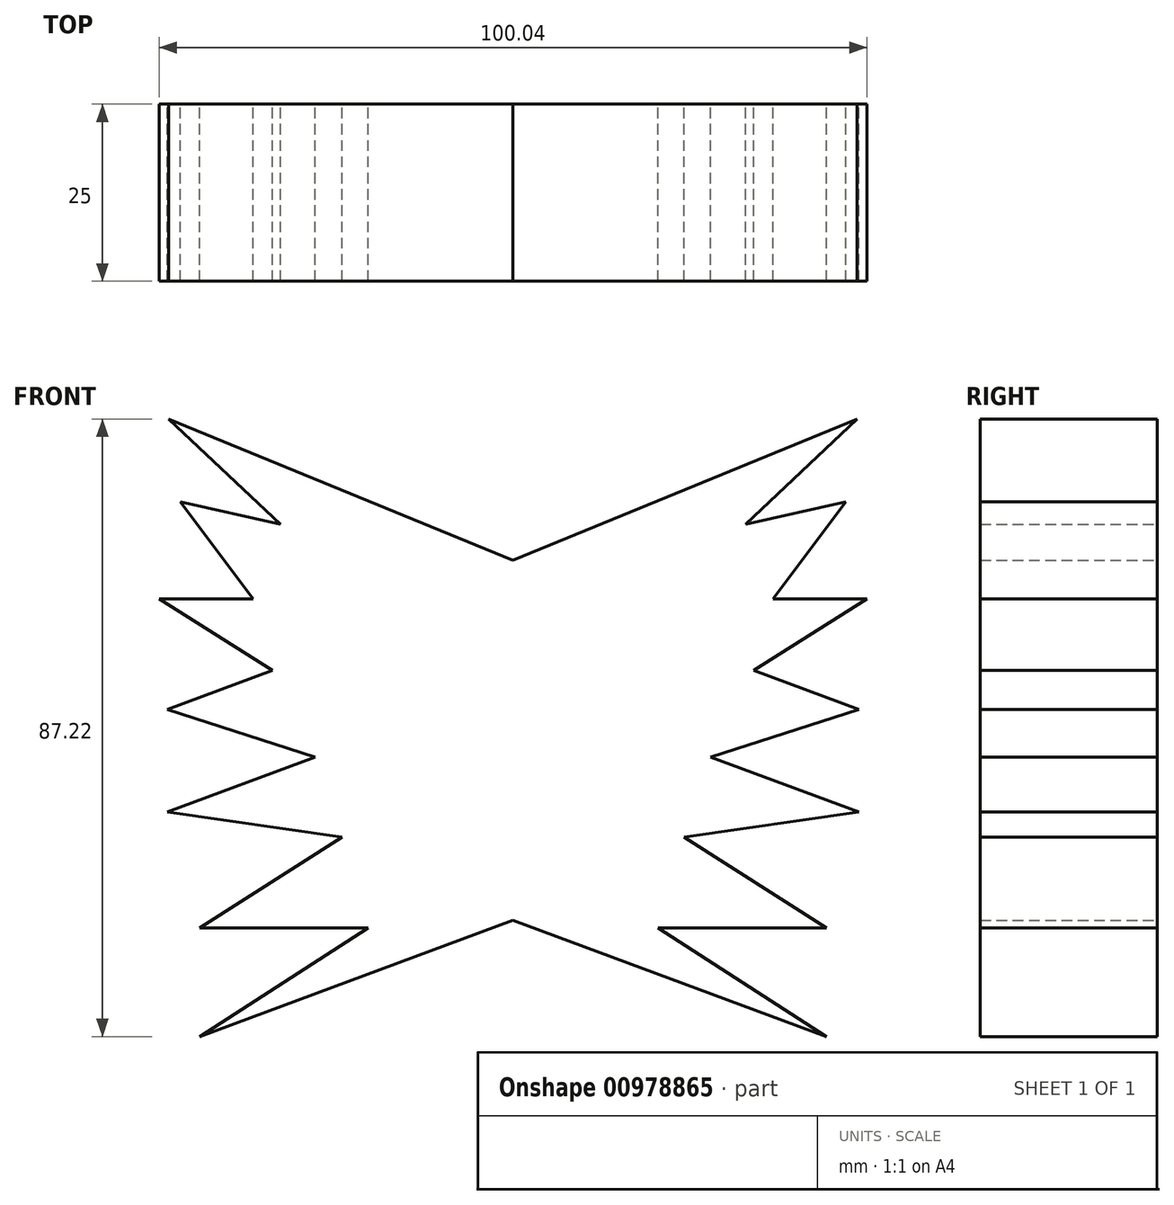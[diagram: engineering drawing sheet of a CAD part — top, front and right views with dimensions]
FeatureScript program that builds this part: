
annotation { "Feature Type Name" : "Feature", "Feature Type Description" : "" }
export const myFeature = defineFeature(function(context is Context, id is Id, definition is map)
    precondition{}
    {
        {
            var Q0;
            Q0=qCreatedBy(makeId("Front.planeOp"),FACE);
            var sketch = newSketch(context, id + "F0", { "sketchPlane" : qUnion([Q0])});
            skLineSegment(sketch, "E0", {"start": v(0, 35.6) * mm, "end": v(-48.65, 55.51) * mm});
            skLineSegment(sketch, "E1", {"start": v(-48.65, 55.51) * mm, "end": v(-32.85, 40.63) * mm});
            skLineSegment(sketch, "E2", {"start": v(-32.85, 40.63) * mm, "end": v(-47.04, 43.84) * mm});
            skLineSegment(sketch, "E3", {"start": v(-47.04, 43.84) * mm, "end": v(-36.74, 30.1) * mm});
            skLineSegment(sketch, "E4", {"start": v(-36.74, 30.1) * mm, "end": v(-50.02, 30.1) * mm});
            skLineSegment(sketch, "E5", {"start": v(-50.02, 30.1) * mm, "end": v(-34, 20.03) * mm});
            skLineSegment(sketch, "E6", {"start": v(-34, 20.03) * mm, "end": v(-48.88, 14.52) * mm});
            skLineSegment(sketch, "E7", {"start": v(-48.88, 14.52) * mm, "end": v(-27.94, 7.75) * mm});
            skLineSegment(sketch, "E8", {"start": v(-27.94, 7.75) * mm, "end": v(-48.88, 0) * mm});
            skLineSegment(sketch, "E9", {"start": v(-48.88, 0) * mm, "end": v(-24.15, -3.55) * mm});
            skLineSegment(sketch, "E10", {"start": v(-24.15, -3.55) * mm, "end": v(-44.3, -16.37) * mm});
            skLineSegment(sketch, "E11", {"start": v(-44.3, -16.37) * mm, "end": v(-20.49, -16.37) * mm});
            skLineSegment(sketch, "E12", {"start": v(-20.49, -16.37) * mm, "end": v(-44.3, -31.7) * mm});
            skLineSegment(sketch, "E13", {"start": v(-44.3, -31.7) * mm, "end": v(0, -15.31) * mm});
            skLineSegment(sketch, "E14", {"start": v(0, 60.32) * mm, "end": v(0, -32.62) * mm});
            skLineSegment(sketch, "E15.MirrorCS", {"start": v(0, 35.6) * mm, "end": v(48.65, 55.51) * mm});
            skLineSegment(sketch, "E16.MirrorCS", {"start": v(48.65, 55.51) * mm, "end": v(32.85, 40.63) * mm});
            skLineSegment(sketch, "E17.MirrorCS", {"start": v(32.85, 40.63) * mm, "end": v(47.04, 43.84) * mm});
            skLineSegment(sketch, "E18.MirrorCS", {"start": v(47.04, 43.84) * mm, "end": v(36.74, 30.1) * mm});
            skLineSegment(sketch, "E19.MirrorCS", {"start": v(36.74, 30.1) * mm, "end": v(50.02, 30.1) * mm});
            skLineSegment(sketch, "E20.MirrorCS", {"start": v(50.02, 30.1) * mm, "end": v(34, 20.03) * mm});
            skLineSegment(sketch, "E21.MirrorCS", {"start": v(34, 20.03) * mm, "end": v(48.88, 14.52) * mm});
            skLineSegment(sketch, "E22.MirrorCS", {"start": v(48.88, 14.52) * mm, "end": v(27.94, 7.75) * mm});
            skLineSegment(sketch, "E23.MirrorCS", {"start": v(27.94, 7.75) * mm, "end": v(48.88, 0) * mm});
            skLineSegment(sketch, "E24.MirrorCS", {"start": v(48.88, 0) * mm, "end": v(24.15, -3.55) * mm});
            skLineSegment(sketch, "E25.MirrorCS", {"start": v(24.15, -3.55) * mm, "end": v(44.3, -16.37) * mm});
            skLineSegment(sketch, "E26.MirrorCS", {"start": v(44.3, -16.37) * mm, "end": v(20.49, -16.37) * mm});
            skLineSegment(sketch, "E27.MirrorCS", {"start": v(20.49, -16.37) * mm, "end": v(44.3, -31.7) * mm});
            skLineSegment(sketch, "E28.MirrorCS", {"start": v(44.3, -31.7) * mm, "end": v(0, -15.31) * mm});
            skSolve(sketch);
        }
        {
            var Q0;
            {var subQ0=sQuery(id+"F0.wireOp",EDGE,"E15.MirrorCS");Q0=makeQuery(id+"F0.imprint","IMPRINT",FACE,{"disambiguationData":[TD([[makeQuery(id+"F0.imprint","IMPRINT",EDGE,{"derivedFrom":subQ0}),-1.0]])]});}
            var Q1;
            {var subQ0=sQuery(id+"F0.wireOp",EDGE,"E0");Q1=makeQuery(id+"F0.imprint","IMPRINT",FACE,{"disambiguationData":[TD([[makeQuery(id+"F0.imprint","IMPRINT",EDGE,{"derivedFrom":subQ0}),1.0]])]});}
            extrude(context, id + "F1", {"entities" : qUnion([Q0, Q1]), "depth" : 25 * mm, "offsetDistance" : 25 * mm});
        }
    });
